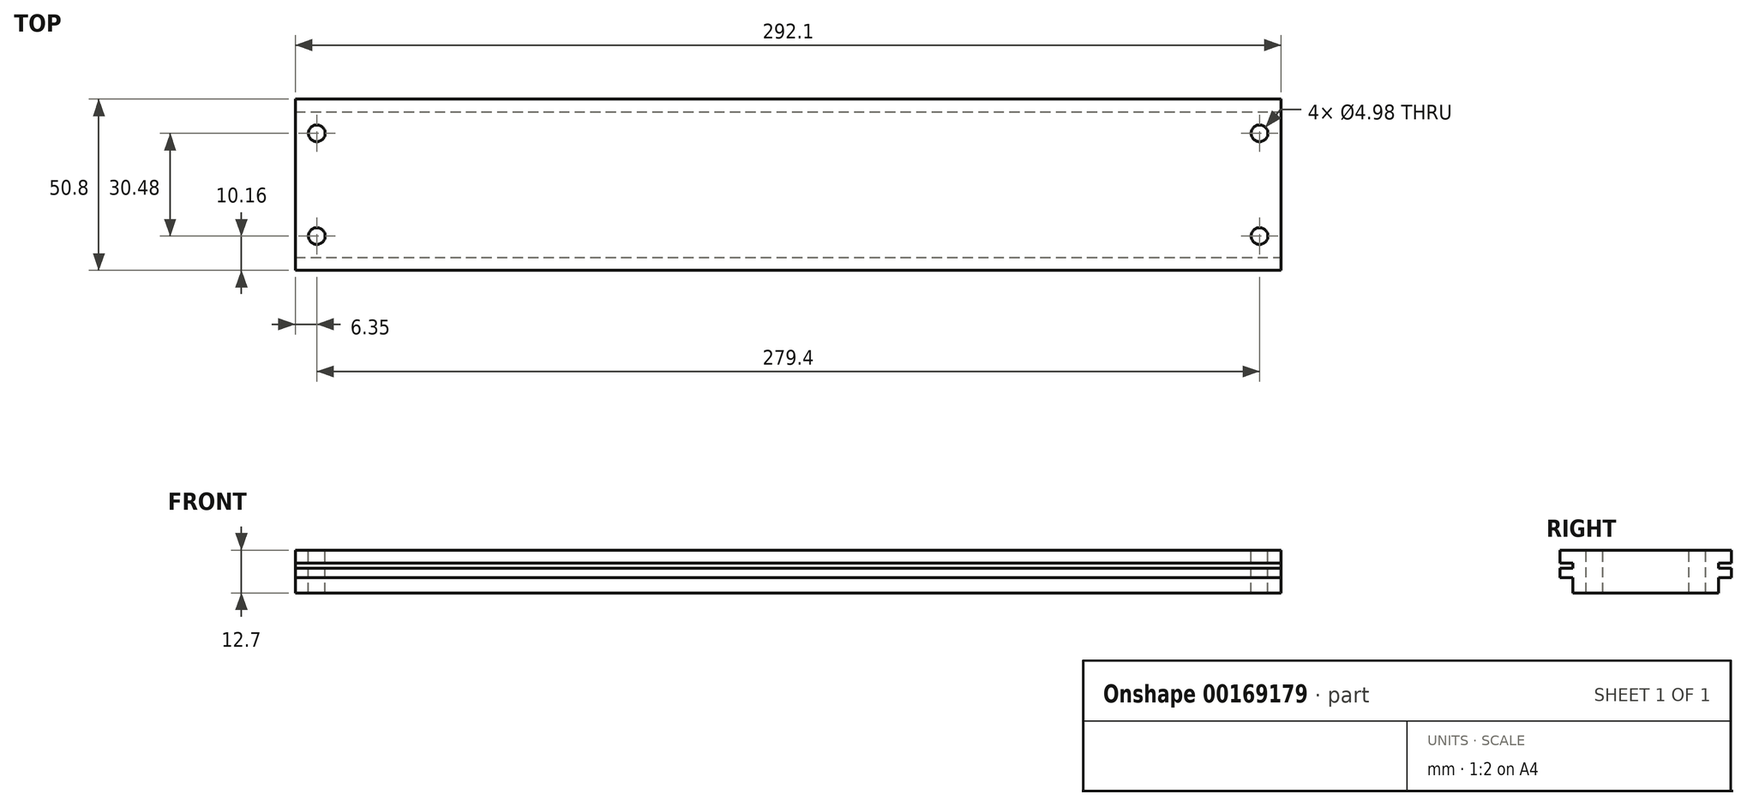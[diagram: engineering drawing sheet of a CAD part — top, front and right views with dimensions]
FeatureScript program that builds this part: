
annotation { "Feature Type Name" : "Feature", "Feature Type Description" : "" }
export const myFeature = defineFeature(function(context is Context, id is Id, definition is map)
    precondition{}
    {
        {
            var Q0;
            Q0=qCreatedBy(makeId("Top.planeOp"),FACE);
            var sketch = newSketch(context, id + "F0", { "sketchPlane" : qUnion([Q0])});
            skLineSegment(sketch, "E0.bottom", {"start": v(0, 0) * mm, "end": v(292.1, 0) * mm});
            skLineSegment(sketch, "E0.top", {"start": v(0, 50.8) * mm, "end": v(292.1, 50.8) * mm});
            skLineSegment(sketch, "E0.left", {"start": v(0, 0) * mm, "end": v(0, 50.8) * mm});
            skLineSegment(sketch, "E0.right", {"start": v(292.1, 0) * mm, "end": v(292.1, 50.8) * mm});
            skPoint(sketch, "E1", {"position": v(6.35, 40.64) * mm});
            skPoint(sketch, "E2", {"position": v(6.35, 10.16) * mm});
            skPoint(sketch, "E3", {"position": v(285.75, 40.64) * mm});
            skPoint(sketch, "E4", {"position": v(285.75, 10.16) * mm});
            skSolve(sketch);
        }
        {
            var Q0;
            Q0=makeQuery(id+"F0.imprint","IMPRINT",FACE,{"disambiguationData":[TD([[makeQuery(id+"F0.imprint","IMPRINT",EDGE,{"derivedFrom":sQuery(id+"F0.wireOp",EDGE,"E0.bottom")}),1.0]])]});
            extrude(context, id + "F1", {"entities" : qUnion([Q0]), "oppositeDirection" : true, "depth" : 12.7 * mm});
        }
        {
            var Q0;
            Q0=sQuery(id+"F0.wireOp",EDGE,"E0.right");
            cPoint(context, id + "F2", {"entities" : qUnion([Q0]), "parameter" : 0.5});
        }
        {
            var Q0;
            Q0=makeQuery(id+"F1.opExtrude","CAP_EDGE",EDGE,{"disambiguationData":[OSD([sQuery(id+"F0.wireOp",EDGE,"E0.right")])],"isStart":false});
            cPoint(context, id + "F3", {"entities" : qUnion([Q0]), "parameter" : 0.5});
        }
        {
            var Q0;
            Q0=sQuery(id+"F0.wireOp",EDGE,"E0.left");
            cPoint(context, id + "F4", {"entities" : qUnion([Q0]), "parameter" : 0.5});
        }
        {
            var Q0;
            Q0 = qCreatedBy(id + "F2" ,VERTEX);
            var Q1;
            Q1 = qCreatedBy(id + "F3" ,VERTEX);
            var Q2;
            Q2 = qCreatedBy(id + "F4" ,VERTEX);
            cPlane(context, id + "F5", {"entities" : qUnion([Q0, Q1, Q2]), "cplaneType" : CPlaneType.THREE_POINT, "offset" : 25.4 * mm, "width" : 152.4 * mm, "height" : 152.4 * mm});
        }
        {
            var Q0;
            Q0=sQuery(id+"F0.wireOp",VERTEX,"E1");
            var Q1;
            Q1=sQuery(id+"F0.wireOp",VERTEX,"E3");
            var Q2;
            Q2=sQuery(id+"F0.wireOp",VERTEX,"E4");
            var Q3;
            Q3=sQuery(id+"F0.wireOp",VERTEX,"E2");
            var Q4;
            Q4=makeQuery(id+"F1.opExtrude","SWEPT_BODY",BODY,{"disambiguationData":[OSD([sQuery(id+"F0.wireOp",EDGE,"E0.bottom"),sQuery(id+"F0.wireOp",EDGE,"E0.top"),sQuery(id+"F0.wireOp",EDGE,"E0.left"),sQuery(id+"F0.wireOp",EDGE,"E0.right")])]});
            hole(context, id + "F6", {"style" : HoleStyle.SIMPLE, "endStyle" : HoleEndStyle.THROUGH, "standardTappedOrClearance" : lookupTablePath({ "standard" : "ANSI", "fit" : "Close", "size" : "#10", "type" : "Clearance" }), "standardBlindInLast" : lookupTablePath({ "fit" : "Close", "standard" : "ANSI", "size" : "#10", "type" : "Clearance" }), "holeDiameter" : 4.98 * mm, "startFromSketch" : true, "locations" : qUnion([Q0, Q1, Q2, Q3]), "scope" : qUnion([Q4]), "isTappedThrough" : true});
        }
        {
            var Q0;
            Q0=makeQuery(id+"F1.opExtrude","SWEPT_FACE",FACE,{"disambiguationData":[OSD([sQuery(id+"F0.wireOp",EDGE,"E0.right")])]});
            var sketch = newSketch(context, id + "F7", { "sketchPlane" : qUnion([Q0])});
            skLineSegment(sketch, "E5", {"start": v(-30.83, -23.46) * mm, "end": v(-14.32, -23.46) * mm});
            skLineSegment(sketch, "E6", {"start": v(-14.32, -23.46) * mm, "end": v(-14.32, -10.76) * mm});
            skLineSegment(sketch, "E7", {"start": v(-14.32, -10.76) * mm, "end": v(-22.62, -10.76) * mm});
            skLineSegment(sketch, "E8", {"start": v(-22.62, -10.76) * mm, "end": v(-22.62, -9.36) * mm});
            skLineSegment(sketch, "E9", {"start": v(-22.62, -9.36) * mm, "end": v(-25.42, -9.36) * mm});
            skLineSegment(sketch, "E10", {"start": v(-25.42, -9.36) * mm, "end": v(-25.42, -10.76) * mm});
            skLineSegment(sketch, "E11", {"start": v(-25.42, -10.76) * mm, "end": v(-30.83, -10.76) * mm});
            skLineSegment(sketch, "E12", {"start": v(-30.83, -10.76) * mm, "end": v(-30.83, -23.46) * mm});
            skLineSegment(sketch, "E13", {"start": v(-30.83, -10.76) * mm, "end": v(-30.83, -6.95) * mm});
            skLineSegment(sketch, "E14", {"start": v(-30.83, -6.95) * mm, "end": v(-27.02, -6.95) * mm});
            skLineSegment(sketch, "E15", {"start": v(-27.02, -6.95) * mm, "end": v(-27.02, -10.76) * mm});
            skLineSegment(sketch, "E16.bottom", {"start": v(0, -3.81) * mm, "end": v(3.81, -3.81) * mm});
            skLineSegment(sketch, "E16.top", {"start": v(0, -5.41) * mm, "end": v(3.81, -5.41) * mm});
            skLineSegment(sketch, "E16.left", {"start": v(0, -3.81) * mm, "end": v(0, -5.41) * mm});
            skLineSegment(sketch, "E16.right", {"start": v(3.81, -3.81) * mm, "end": v(3.81, -5.41) * mm});
            skLineSegment(sketch, "E17.bottom", {"start": v(0, -5.41) * mm, "end": v(2.41, -5.41) * mm});
            skLineSegment(sketch, "E17.top", {"start": v(0, -8.21) * mm, "end": v(2.41, -8.21) * mm});
            skLineSegment(sketch, "E17.left", {"start": v(0, -5.41) * mm, "end": v(0, -8.21) * mm});
            skLineSegment(sketch, "E17.right", {"start": v(2.41, -5.41) * mm, "end": v(2.41, -8.21) * mm});
            skLineSegment(sketch, "E18.bottom", {"start": v(0, -8.21) * mm, "end": v(3.81, -8.21) * mm});
            skLineSegment(sketch, "E18.top", {"start": v(0, -12.7) * mm, "end": v(3.81, -12.7) * mm});
            skLineSegment(sketch, "E18.left", {"start": v(0, -8.21) * mm, "end": v(0, -12.7) * mm});
            skLineSegment(sketch, "E18.right", {"start": v(3.81, -8.21) * mm, "end": v(3.81, -12.7) * mm});
            skLineSegment(sketch, "E19.MirrorCS", {"start": v(50.8, -8.21) * mm, "end": v(47, -8.21) * mm});
            skLineSegment(sketch, "E20.MirrorCS", {"start": v(50.8, -5.41) * mm, "end": v(48.39, -5.41) * mm});
            skLineSegment(sketch, "E21.MirrorCS", {"start": v(50.8, -8.21) * mm, "end": v(50.8, -12.7) * mm});
            skLineSegment(sketch, "E22.MirrorCS", {"start": v(50.8, -5.41) * mm, "end": v(47, -5.41) * mm});
            skLineSegment(sketch, "E23.MirrorCS", {"start": v(50.8, -8.21) * mm, "end": v(48.39, -8.21) * mm});
            skLineSegment(sketch, "E24.MirrorCS", {"start": v(50.8, -5.41) * mm, "end": v(50.8, -8.21) * mm});
            skLineSegment(sketch, "E25.MirrorCS", {"start": v(47, -8.21) * mm, "end": v(47, -12.7) * mm});
            skLineSegment(sketch, "E26.MirrorCS", {"start": v(50.8, -12.7) * mm, "end": v(47, -12.7) * mm});
            skLineSegment(sketch, "E27.MirrorCS", {"start": v(47, -3.81) * mm, "end": v(47, -5.41) * mm});
            skLineSegment(sketch, "E28.MirrorCS", {"start": v(48.39, -5.41) * mm, "end": v(48.39, -8.21) * mm});
            skLineSegment(sketch, "E29.MirrorCS", {"start": v(50.8, -3.81) * mm, "end": v(47, -3.81) * mm});
            skLineSegment(sketch, "E30.MirrorCS", {"start": v(50.8, -3.81) * mm, "end": v(50.8, -5.41) * mm});
            skSolve(sketch);
        }
        {
            var Q0;
            Q0=makeQuery(id+"F7.imprint","IMPRINT",FACE,{"disambiguationData":[TD([[makeQuery(id+"F7.imprint","IMPRINT",EDGE,{"derivedFrom":sQuery(id+"F7.wireOp",EDGE,"E16.bottom")}),-1.0]])]});
            var Q1;
            Q1=makeQuery(id+"F7.imprint","IMPRINT",FACE,{"disambiguationData":[TD([[makeQuery(id+"F7.imprint","IMPRINT",EDGE,{"derivedFrom":sQuery(id+"F7.wireOp",EDGE,"E17.bottom")}),-1.0]])]});
            var Q2;
            Q2=makeQuery(id+"F7.imprint","IMPRINT",FACE,{"disambiguationData":[TD([[makeQuery(id+"F7.imprint","IMPRINT",EDGE,{"derivedFrom":sQuery(id+"F7.wireOp",EDGE,"E18.top")}),1.0]])]});
            var Q3;
            {var subQ0=sQuery(id+"F7.wireOp",EDGE,"E27.MirrorCS");Q3=makeQuery(id+"F7.imprint","IMPRINT",FACE,{"disambiguationData":[TD([[makeQuery(id+"F7.imprint","IMPRINT",EDGE,{"derivedFrom":subQ0}),1.0]])]});}
            var Q4;
            Q4=makeQuery(id+"F7.imprint","IMPRINT",FACE,{"disambiguationData":[TD([[makeQuery(id+"F7.imprint","IMPRINT",EDGE,{"derivedFrom":sQuery(id+"F7.wireOp",EDGE,"E23.MirrorCS")}),-1.0]])]});
            var Q5;
            Q5=makeQuery(id+"F7.imprint","IMPRINT",FACE,{"disambiguationData":[TD([[makeQuery(id+"F7.imprint","IMPRINT",EDGE,{"derivedFrom":sQuery(id+"F7.wireOp",EDGE,"E19.MirrorCS")}),1.0]])]});
            extrude(context, id + "F8", {"entities" : qUnion([Q0, Q1, Q2, Q3, Q4, Q5]), "operationType" : NewBodyOperationType.REMOVE, "endBound" : BoundingType.UP_TO_NEXT, "oppositeDirection" : true, "depth" : 25.4 * mm});
        }
    });
